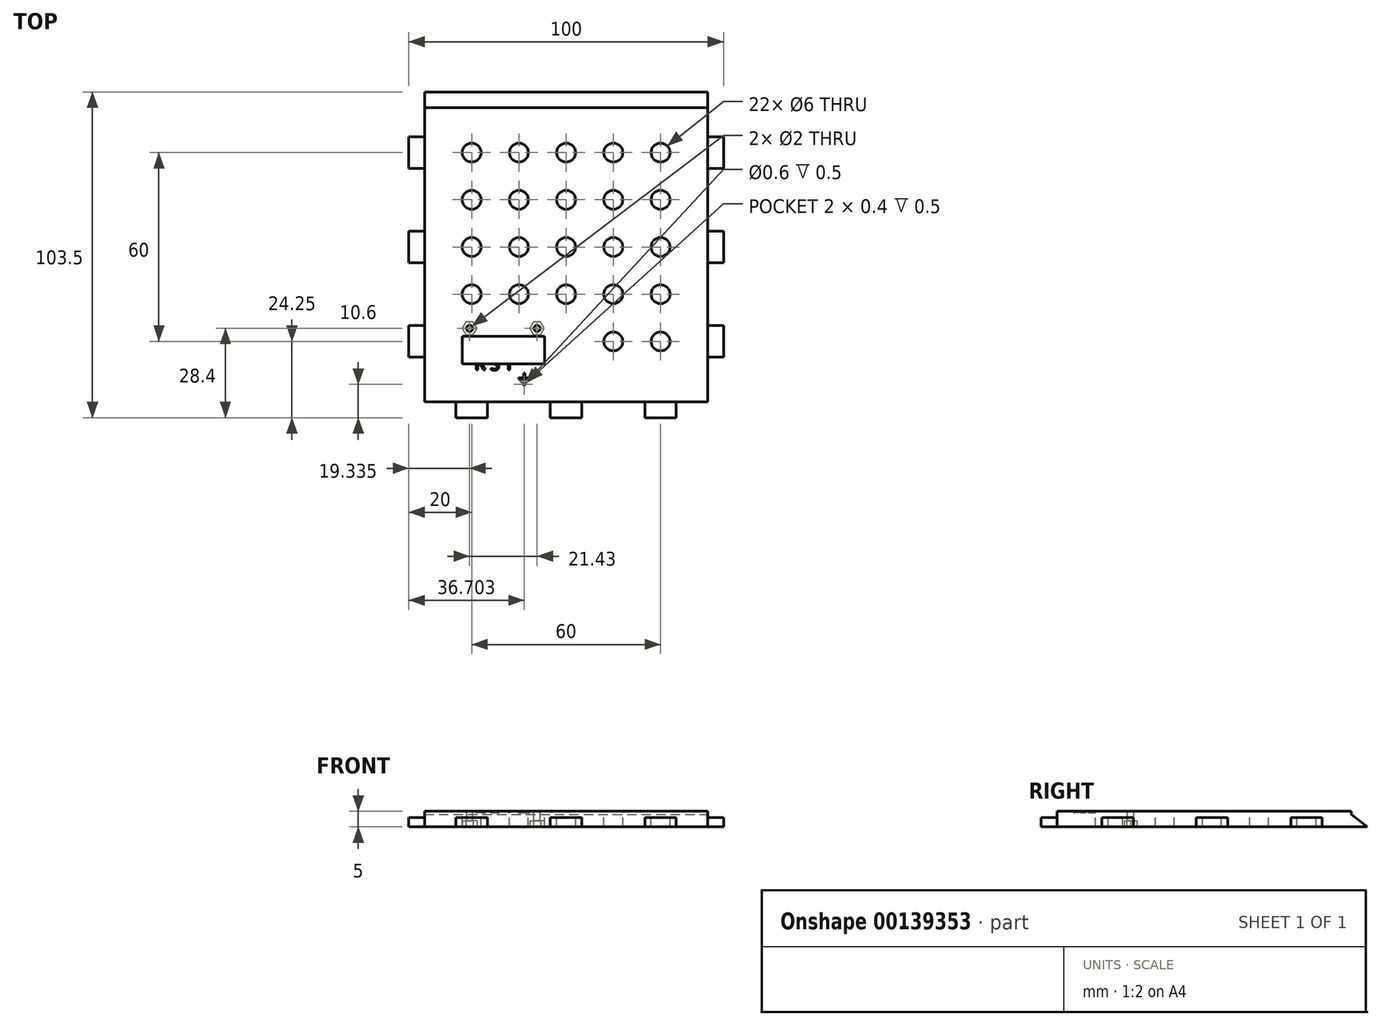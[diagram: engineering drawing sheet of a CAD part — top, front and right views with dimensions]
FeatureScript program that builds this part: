
annotation { "Feature Type Name" : "Feature", "Feature Type Description" : "" }
export const myFeature = defineFeature(function(context is Context, id is Id, definition is map)
    precondition{}
    {
        {
            var Q0;
            Q0=qCreatedBy(makeId("Top.planeOp"),FACE);
            var sketch = newSketch(context, id + "F0", { "sketchPlane" : qUnion([Q0])});
            skLineSegment(sketch, "E0.bottom", {"start": v(45, 49.25) * mm, "end": v(-45, 49.25) * mm});
            skLineSegment(sketch, "E0.top", {"start": v(45, -49.25) * mm, "end": v(-45, -49.25) * mm});
            skLineSegment(sketch, "E0.left", {"start": v(45, 49.25) * mm, "end": v(45, -49.25) * mm});
            skLineSegment(sketch, "E0.right", {"start": v(-45, 49.25) * mm, "end": v(-45, -49.25) * mm});
            skPoint(sketch, "E0.middle", {"position": v(0, 0) * mm});
            skSolve(sketch);
        }
        {
            var Q0;
            Q0 = qSketchRegion(id + "F0", true);
            extrude(context, id + "F1", {"entities" : qUnion([Q0]), "depth" : 5 * mm});
        }
        {
            var Q0;
            Q0=makeQuery(id+"F1.opExtrude","SWEPT_FACE",FACE,{"disambiguationData":[OSD([sQuery(id+"F0.wireOp",EDGE,"E0.left")])]});
            var sketch = newSketch(context, id + "F2", { "sketchPlane" : qUnion([Q0])});
            skLineSegment(sketch, "E1", {"start": v(49.25, 5) * mm, "end": v(44.25, 5) * mm});
            skLineSegment(sketch, "E2", {"start": v(44.25, 5) * mm, "end": v(44.25, 4) * mm});
            skLineSegment(sketch, "E3", {"start": v(44.25, 4) * mm, "end": v(49.25, 0) * mm});
            skSolve(sketch);
        }
        {
            var Q0;
            Q0=makeQuery(id+"F2.imprint","IMPRINT",FACE,{"disambiguationData":[TD([[makeQuery(id+"F2.imprint","IMPRINT",EDGE,{"derivedFrom":sQuery(id+"F2.wireOp",EDGE,"E1")}),1.0]])]});
            extrude(context, id + "F3", {"entities" : qUnion([Q0]), "operationType" : NewBodyOperationType.REMOVE, "oppositeDirection" : true, "depth" : 100 * mm});
        }
        {
            var Q0;
            Q0=makeQuery(id+"F1.opExtrude","SWEPT_FACE",FACE,{"disambiguationData":[OSD([sQuery(id+"F0.wireOp",EDGE,"E0.left")])]});
            var sketch = newSketch(context, id + "F4", { "sketchPlane" : qUnion([Q0])});
            skLineSegment(sketch, "E4.bottom", {"start": v(-35, 0) * mm, "end": v(-25, 0) * mm});
            skLineSegment(sketch, "E4.top", {"start": v(-35, 3) * mm, "end": v(-25, 3) * mm});
            skLineSegment(sketch, "E4.left", {"start": v(-35, 0) * mm, "end": v(-35, 3) * mm});
            skLineSegment(sketch, "E4.right", {"start": v(-25, 0) * mm, "end": v(-25, 3) * mm});
            skLineSegment(sketch, "E5.bottom", {"start": v(-5, 0) * mm, "end": v(5, 0) * mm});
            skLineSegment(sketch, "E5.top", {"start": v(-5, 3) * mm, "end": v(5, 3) * mm});
            skLineSegment(sketch, "E5.left", {"start": v(-5, 0) * mm, "end": v(-5, 3) * mm});
            skLineSegment(sketch, "E5.right", {"start": v(5, 0) * mm, "end": v(5, 3) * mm});
            skLineSegment(sketch, "E6.bottom", {"start": v(25, 0) * mm, "end": v(35, 0) * mm});
            skLineSegment(sketch, "E6.top", {"start": v(25, 3) * mm, "end": v(35, 3) * mm});
            skLineSegment(sketch, "E6.left", {"start": v(25, 0) * mm, "end": v(25, 3) * mm});
            skLineSegment(sketch, "E6.right", {"start": v(35, 0) * mm, "end": v(35, 3) * mm});
            skSolve(sketch);
        }
        {
            var Q0;
            Q0=makeQuery(id+"F4.imprint","IMPRINT",FACE,{"disambiguationData":[TD([[makeQuery(id+"F4.imprint","IMPRINT",EDGE,{"derivedFrom":sQuery(id+"F4.wireOp",EDGE,"E5.bottom")}),-1.0]])]});
            var Q1;
            Q1=makeQuery(id+"F4.imprint","IMPRINT",FACE,{"disambiguationData":[TD([[makeQuery(id+"F4.imprint","IMPRINT",EDGE,{"derivedFrom":sQuery(id+"F4.wireOp",EDGE,"E6.bottom")}),-1.0]])]});
            var Q2;
            Q2=makeQuery(id+"F4.imprint","IMPRINT",FACE,{"disambiguationData":[TD([[makeQuery(id+"F4.imprint","IMPRINT",EDGE,{"derivedFrom":sQuery(id+"F4.wireOp",EDGE,"E4.bottom")}),-1.0]])]});
            extrude(context, id + "F5", {"entities" : qUnion([Q0, Q1, Q2]), "operationType" : NewBodyOperationType.ADD, "oppositeDirection" : true, "depth" : 95 * mm, "hasSecondDirection" : true, "secondDirectionOppositeDirection" : false, "secondDirectionDepth" : 5 * mm});
        }
        {
            var Q0;
            Q0=makeQuery(id+"F1.opExtrude","SWEPT_FACE",FACE,{"disambiguationData":[OSD([sQuery(id+"F0.wireOp",EDGE,"E0.top")])]});
            var sketch = newSketch(context, id + "F6", { "sketchPlane" : qUnion([Q0])});
            skLineSegment(sketch, "E7.bottom", {"start": v(-35, 0) * mm, "end": v(-25, 0) * mm});
            skLineSegment(sketch, "E7.top", {"start": v(-35, 3) * mm, "end": v(-25, 3) * mm});
            skLineSegment(sketch, "E7.left", {"start": v(-35, 0) * mm, "end": v(-35, 3) * mm});
            skLineSegment(sketch, "E7.right", {"start": v(-25, 0) * mm, "end": v(-25, 3) * mm});
            skLineSegment(sketch, "E8.bottom", {"start": v(-5, 0) * mm, "end": v(5, 0) * mm});
            skLineSegment(sketch, "E8.top", {"start": v(-5, 3) * mm, "end": v(5, 3) * mm});
            skLineSegment(sketch, "E8.left", {"start": v(-5, 0) * mm, "end": v(-5, 3) * mm});
            skLineSegment(sketch, "E8.right", {"start": v(5, 0) * mm, "end": v(5, 3) * mm});
            skLineSegment(sketch, "E9.bottom", {"start": v(25, 0) * mm, "end": v(35, 0) * mm});
            skLineSegment(sketch, "E9.top", {"start": v(25, 3) * mm, "end": v(35, 3) * mm});
            skLineSegment(sketch, "E9.left", {"start": v(25, 0) * mm, "end": v(25, 3) * mm});
            skLineSegment(sketch, "E9.right", {"start": v(35, 0) * mm, "end": v(35, 3) * mm});
            skSolve(sketch);
        }
        {
            var Q0;
            Q0 = qSketchRegion(id + "F6", true);
            extrude(context, id + "F7", {"entities" : qUnion([Q0]), "operationType" : NewBodyOperationType.ADD, "depth" : 5 * mm});
        }
        {
            var Q0;
            Q0=makeQuery(id+"F1.opExtrude","CAP_FACE",FACE,{"disambiguationData":[OSD([sQuery(id+"F0.wireOp",EDGE,"E0.bottom"),sQuery(id+"F0.wireOp",EDGE,"E0.top"),sQuery(id+"F0.wireOp",EDGE,"E0.left"),sQuery(id+"F0.wireOp",EDGE,"E0.right")])],"isStart":false});
            var sketch = newSketch(context, id + "F8", { "sketchPlane" : qUnion([Q0])});
            skLineSegment(sketch, "E10.bottom", {"start": v(-33, -28.4) * mm, "end": v(-6.9, -28.4) * mm});
            skLineSegment(sketch, "E10.top", {"start": v(-33, -37.1) * mm, "end": v(-6.9, -37.1) * mm});
            skLineSegment(sketch, "E10.left", {"start": v(-33, -28.4) * mm, "end": v(-33, -37.1) * mm});
            skLineSegment(sketch, "E10.right", {"start": v(-6.9, -28.4) * mm, "end": v(-6.9, -37.1) * mm});
            skLineSegment(sketch, "E11.bottom", {"start": v(-34.77, -23.05) * mm, "end": v(-5.14, -23.05) * mm});
            skLineSegment(sketch, "E11.top", {"start": v(-34.77, -39.25) * mm, "end": v(-5.14, -39.25) * mm});
            skLineSegment(sketch, "E11.left", {"start": v(-34.77, -23.05) * mm, "end": v(-34.77, -39.25) * mm});
            skLineSegment(sketch, "E11.right", {"start": v(-5.14, -23.05) * mm, "end": v(-5.14, -39.25) * mm});
            skCircle(sketch, "E12", {"center": v(-9.24, -25.85) * mm, "radius": 1 * mm});
            skCircle(sketch, "E13", {"center": v(-30.67, -25.85) * mm, "radius": 1 * mm});
            skSolve(sketch);
        }
        {
            var Q0;
            Q0=makeQuery(id+"F8.imprint","IMPRINT",FACE,{"disambiguationData":[TD([[makeQuery(id+"F8.imprint","IMPRINT",EDGE,{"derivedFrom":sQuery(id+"F8.wireOp",EDGE,"E10.bottom")}),-1.0]])]});
            var Q1;
            Q1=makeQuery(id+"F8.imprint","IMPRINT",FACE,{"disambiguationData":[TD([[makeQuery(id+"F8.imprint","IMPRINT",EDGE,{"derivedFrom":sQuery(id+"F8.wireOp",EDGE,"E13")}),1.0]])]});
            var Q2;
            Q2=makeQuery(id+"F8.imprint","IMPRINT",FACE,{"disambiguationData":[TD([[makeQuery(id+"F8.imprint","IMPRINT",EDGE,{"derivedFrom":sQuery(id+"F8.wireOp",EDGE,"E12")}),1.0]])]});
            extrude(context, id + "F9", {"entities" : qUnion([Q0, Q1, Q2]), "operationType" : NewBodyOperationType.REMOVE, "oppositeDirection" : true, "depth" : 25 * mm});
        }
        {
            var Q0;
            Q0=makeQuery(id+"F1.opExtrude","CAP_FACE",FACE,{"disambiguationData":[OSD([sQuery(id+"F0.wireOp",EDGE,"E0.bottom"),sQuery(id+"F0.wireOp",EDGE,"E0.top"),sQuery(id+"F0.wireOp",EDGE,"E0.left"),sQuery(id+"F0.wireOp",EDGE,"E0.right")])],"isStart":false});
            var sketch = newSketch(context, id + "F10", { "sketchPlane" : qUnion([Q0])});
            skText(sketch, "E14", { "text": "R S T", "fontName": "OpenSans-Regular.ttf"});
            skCircle(sketch, "E15", {"center": v(-13.3, -43.65) * mm, "radius": 0.3 * mm});
            skLineSegment(sketch, "E16.bottom", {"start": v(-14.3, -42.5) * mm, "end": v(-12.3, -42.5) * mm});
            skLineSegment(sketch, "E16.top", {"start": v(-14.3, -42.9) * mm, "end": v(-12.3, -42.9) * mm});
            skLineSegment(sketch, "E16.left", {"start": v(-14.3, -42.5) * mm, "end": v(-14.3, -42.9) * mm});
            skLineSegment(sketch, "E16.right", {"start": v(-12.3, -42.5) * mm, "end": v(-12.3, -42.9) * mm});
            skLineSegment(sketch, "E17.bottom", {"start": v(-15.05, -41.6) * mm, "end": v(-11.55, -41.6) * mm});
            skLineSegment(sketch, "E17.top", {"start": v(-15.05, -42) * mm, "end": v(-11.55, -42) * mm});
            skLineSegment(sketch, "E17.left", {"start": v(-15.05, -41.6) * mm, "end": v(-15.05, -42) * mm});
            skLineSegment(sketch, "E17.right", {"start": v(-11.55, -41.6) * mm, "end": v(-11.55, -42) * mm});
            skLineSegment(sketch, "E18.bottom", {"start": v(-13.1, -41.6) * mm, "end": v(-13.5, -41.6) * mm});
            skLineSegment(sketch, "E18.top", {"start": v(-13.1, -40.1) * mm, "end": v(-13.5, -40.1) * mm});
            skLineSegment(sketch, "E18.left", {"start": v(-13.1, -41.6) * mm, "end": v(-13.1, -40.1) * mm});
            skLineSegment(sketch, "E18.right", {"start": v(-13.5, -41.6) * mm, "end": v(-13.5, -40.1) * mm});
            const initialGuessF10  = {"E14": [-0.02904, -0.0391, 1, 0, 0.004]};
            skSetInitialGuess(sketch, initialGuessF10);
            skSolve(sketch);
        }
        {
            var Q0;
            Q0 = qSketchRegion(id + "F10", true);
            extrude(context, id + "F11", {"entities" : qUnion([Q0]), "operationType" : NewBodyOperationType.REMOVE, "oppositeDirection" : true, "depth" : 0.5 * mm});
        }
        {
            var Q0;
            {var subQ0=sQuery(id+"F0.wireOp",EDGE,"E0.top");var subQ1=sQuery(id+"F0.wireOp",EDGE,"E0.left");var subQ2=sQuery(id+"F0.wireOp",EDGE,"E0.right");Q0=makeQuery(id+"F11.boolean.opBoolean","SPLIT",FACE,{"disambiguationData":[TD([makeQuery(id+"F1.opExtrude","SWEPT_FACE",FACE,{"disambiguationData":[OSD([subQ0])]})])],"derivedFrom":makeQuery(id+"F1.opExtrude","CAP_FACE",FACE,{"disambiguationData":[OSD([sQuery(id+"F0.wireOp",EDGE,"E0.bottom"),subQ0,subQ1,subQ2])],"isStart":false})});}
            var sketch = newSketch(context, id + "F12", { "sketchPlane" : qUnion([Q0])});
            skCircle(sketch, "E19", {"center": v(-30, 30) * mm, "radius": 3 * mm});
            skCircle(sketch, "E20.0.1.0", {"center": v(-30, 15) * mm, "radius": 3 * mm});
            skCircle(sketch, "E20.0.2.0", {"center": v(-30, 0) * mm, "radius": 3 * mm});
            skCircle(sketch, "E20.0.3.0", {"center": v(-30, -15) * mm, "radius": 3 * mm});
            skCircle(sketch, "E20.1.0.0", {"center": v(-15, 30) * mm, "radius": 3 * mm});
            skCircle(sketch, "E20.1.1.0", {"center": v(-15, 15) * mm, "radius": 3 * mm});
            skCircle(sketch, "E20.1.2.0", {"center": v(-15, 0) * mm, "radius": 3 * mm});
            skCircle(sketch, "E20.1.3.0", {"center": v(-15, -15) * mm, "radius": 3 * mm});
            skCircle(sketch, "E20.2.0.0", {"center": v(0, 30) * mm, "radius": 3 * mm});
            skCircle(sketch, "E20.2.1.0", {"center": v(0, 15) * mm, "radius": 3 * mm});
            skCircle(sketch, "E20.2.2.0", {"center": v(0, 0) * mm, "radius": 3 * mm});
            skCircle(sketch, "E20.2.3.0", {"center": v(0, -15) * mm, "radius": 3 * mm});
            skCircle(sketch, "E20.3.0.0", {"center": v(15, 30) * mm, "radius": 3 * mm});
            skCircle(sketch, "E20.3.1.0", {"center": v(15, 15) * mm, "radius": 3 * mm});
            skCircle(sketch, "E20.3.2.0", {"center": v(15, 0) * mm, "radius": 3 * mm});
            skCircle(sketch, "E20.3.3.0", {"center": v(15, -15) * mm, "radius": 3 * mm});
            skCircle(sketch, "E20.4.0.0", {"center": v(30, 30) * mm, "radius": 3 * mm});
            skCircle(sketch, "E20.4.1.0", {"center": v(30, 15) * mm, "radius": 3 * mm});
            skCircle(sketch, "E20.4.2.0", {"center": v(30, 0) * mm, "radius": 3 * mm});
            skCircle(sketch, "E20.4.3.0", {"center": v(30, -15) * mm, "radius": 3 * mm});
            skLineSegment(sketch, "E20.direction1", {"start": v(-35, 34.25) * mm, "end": v(-20, 34.25) * mm, "construction": true});
            skLineSegment(sketch, "E20.direction2", {"start": v(-35, 34.25) * mm, "end": v(-35, 19.25) * mm, "construction": true});
            skCircle(sketch, "E21.0.1.0", {"center": v(30, -30) * mm, "radius": 3 * mm});
            skCircle(sketch, "E21.0.1.1", {"center": v(15, -30) * mm, "radius": 3 * mm});
            skLineSegment(sketch, "E21.direction1", {"start": v(15, -15) * mm, "end": v(40, -15) * mm, "construction": true});
            skLineSegment(sketch, "E21.direction2", {"start": v(15, -15) * mm, "end": v(15, -30) * mm, "construction": true});
            skSolve(sketch);
        }
        {
            var Q0;
            Q0 = qSketchRegion(id + "F12", true);
            extrude(context, id + "F13", {"entities" : qUnion([Q0]), "operationType" : NewBodyOperationType.REMOVE, "oppositeDirection" : true, "depth" : 25 * mm});
        }
        {
            var Q0;
            Q0=makeQuery(id+"F7.boolean.opBoolean","MERGE",FACE,{"derivedFrom":[makeQuery(id+"F5.boolean.opBoolean","MERGE",FACE,{"derivedFrom":[makeQuery(id+"F1.opExtrude","CAP_FACE",FACE,{"disambiguationData":[OSD([sQuery(id+"F0.wireOp",EDGE,"E0.bottom"),sQuery(id+"F0.wireOp",EDGE,"E0.top"),sQuery(id+"F0.wireOp",EDGE,"E0.left"),sQuery(id+"F0.wireOp",EDGE,"E0.right")])],"isStart":true}),makeQuery(id+"F5.opExtrude","SWEPT_FACE",FACE,{"disambiguationData":[OSD([sQuery(id+"F4.wireOp",EDGE,"E4.bottom")])]}),makeQuery(id+"F5.opExtrude","SWEPT_FACE",FACE,{"disambiguationData":[OSD([sQuery(id+"F4.wireOp",EDGE,"E5.bottom")])]}),makeQuery(id+"F5.opExtrude","SWEPT_FACE",FACE,{"disambiguationData":[OSD([sQuery(id+"F4.wireOp",EDGE,"E6.bottom")])]})]}),makeQuery(id+"F7.opExtrude","SWEPT_FACE",FACE,{"disambiguationData":[OSD([sQuery(id+"F6.wireOp",EDGE,"E7.bottom")])]}),makeQuery(id+"F7.opExtrude","SWEPT_FACE",FACE,{"disambiguationData":[OSD([sQuery(id+"F6.wireOp",EDGE,"E8.bottom")])]}),makeQuery(id+"F7.opExtrude","SWEPT_FACE",FACE,{"disambiguationData":[OSD([sQuery(id+"F6.wireOp",EDGE,"E9.bottom")])]})]});
            var sketch = newSketch(context, id + "F14", { "sketchPlane" : qUnion([Q0])});
            skCircle(sketch, "E22.cCircle", {"center": v(-30.67, 25.85) * mm, "radius": 2 * mm, "construction": true});
            skLineSegment(sketch, "E22.0", {"start": v(-29.51, 23.85) * mm, "end": v(-31.82, 23.85) * mm});
            skLineSegment(sketch, "E22.1", {"start": v(-31.82, 23.85) * mm, "end": v(-32.97, 25.85) * mm});
            skLineSegment(sketch, "E22.2", {"start": v(-32.97, 25.85) * mm, "end": v(-31.82, 27.85) * mm});
            skLineSegment(sketch, "E22.3", {"start": v(-31.82, 27.85) * mm, "end": v(-29.51, 27.85) * mm});
            skLineSegment(sketch, "E22.4", {"start": v(-29.51, 27.85) * mm, "end": v(-28.36, 25.85) * mm});
            skLineSegment(sketch, "E22.5", {"start": v(-28.36, 25.85) * mm, "end": v(-29.51, 23.85) * mm});
            skPoint(sketch, "E22.0.midPoint", {"position": v(-30.67, 23.85) * mm});
            skCircle(sketch, "E23.cCircle", {"center": v(-9.24, 25.85) * mm, "radius": 2 * mm, "construction": true});
            skLineSegment(sketch, "E23.0", {"start": v(-8.08, 23.85) * mm, "end": v(-10.39, 23.85) * mm});
            skLineSegment(sketch, "E23.1", {"start": v(-10.39, 23.85) * mm, "end": v(-11.54, 25.85) * mm});
            skLineSegment(sketch, "E23.2", {"start": v(-11.54, 25.85) * mm, "end": v(-10.39, 27.85) * mm});
            skLineSegment(sketch, "E23.3", {"start": v(-10.39, 27.85) * mm, "end": v(-8.08, 27.85) * mm});
            skLineSegment(sketch, "E23.4", {"start": v(-8.08, 27.85) * mm, "end": v(-6.93, 25.85) * mm});
            skLineSegment(sketch, "E23.5", {"start": v(-6.93, 25.85) * mm, "end": v(-8.08, 23.85) * mm});
            skPoint(sketch, "E23.0.midPoint", {"position": v(-9.24, 23.85) * mm});
            skSolve(sketch);
        }
        {
            var Q0;
            Q0 = qSketchRegion(id + "F14", true);
            extrude(context, id + "F15", {"entities" : qUnion([Q0]), "operationType" : NewBodyOperationType.REMOVE, "oppositeDirection" : true, "depth" : 2 * mm});
        }
    });
